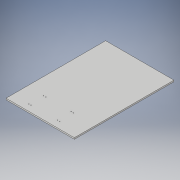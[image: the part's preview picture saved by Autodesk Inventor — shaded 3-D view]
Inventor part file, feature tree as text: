
AUTODESK INVENTOR PART (.ipt)
format: ipt  version: 2019 (Build 230136000, 136)  size: 145,920 bytes
history: native  units: in
note: dims shown in document units (in); Inventor stores cm internally (conversion verified against a paired STEP export)
features: extrude x5, sketch x5, other x1
ambient origin geometry x8: Origin, YZ Plane, XZ Plane, XY Plane, X Axis, Y Axis, Z Axis, Center Point
bodies: Solid1 (feature_tree)
feature tree (11):
  other  "main plate"
  extrude  "Extrusion1"  Depth=17.5in
  extrude  "Extrusion2"  Depth=0.25in
  extrude  "Extrusion3"  Depth=3.746in
  extrude  "Extrusion4"  Depth=1.185in
  extrude  "Extrusion5"  Depth=0.107in
  sketch  "Sketch1"  dims[d0=12.0in d1=17.5in]
  sketch  "Sketch2"  dims[d2=0.25in d3=0.0in d4=0.107in]
  sketch  "Sketch3"  dims[d5=0.107in d7=3.746in]
  sketch  "Sketch4"  dims[d8=0.394in d9=1.185in]
  sketch  "Sketch5"  dims[d10=1.0in d11=0.0in d12=0.107in d13=0.107in d14=2.482in d15=2.482in d16=0.394in d17=3.846in d18=1.0in d19=0.0in d20=0.107in d21=0.107in d22=0.394in d23=2.929in d24=3.665in d25=1.0in d26=0.0in d27=0.107in d28=0.107in d31=1.13in d32=0.394in d34=1.0in d35=0.0in d36=8.741in d37=1.185in d38=1.13in]
